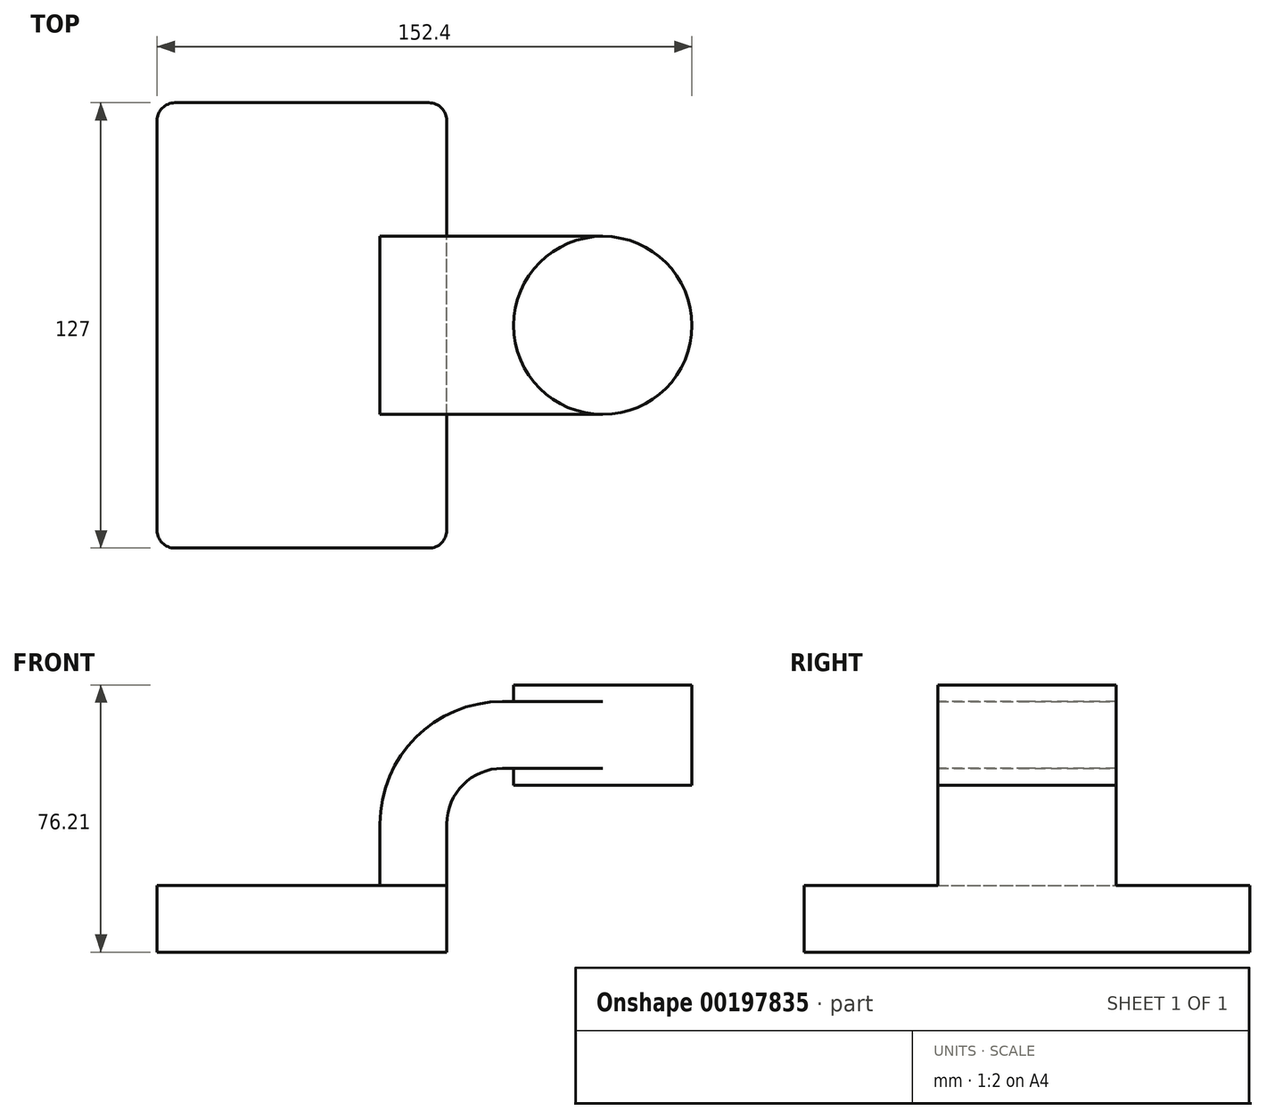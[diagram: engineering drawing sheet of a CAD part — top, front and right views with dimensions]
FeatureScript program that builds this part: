
annotation { "Feature Type Name" : "Feature", "Feature Type Description" : "" }
export const myFeature = defineFeature(function(context is Context, id is Id, definition is map)
    precondition{}
    {
        {
            var Q0;
            Q0=qCreatedBy(makeId("Front.planeOp"),FACE);
            var sketch = newSketch(context, id + "F0", { "sketchPlane" : qUnion([Q0])});
            skLineSegment(sketch, "E0.bottom", {"start": v(41.28, -9.52) * mm, "end": v(-41.27, -9.52) * mm});
            skLineSegment(sketch, "E0.top", {"start": v(41.27, 9.53) * mm, "end": v(-41.28, 9.53) * mm});
            skLineSegment(sketch, "E0.left", {"start": v(41.28, -9.52) * mm, "end": v(41.28, 9.53) * mm});
            skLineSegment(sketch, "E0.right", {"start": v(-41.27, -9.52) * mm, "end": v(-41.28, 9.53) * mm});
            skPoint(sketch, "E0.middle", {"position": v(0, 0) * mm});
            skLineSegment(sketch, "E1.bottom", {"start": v(111.12, 38.1) * mm, "end": v(60.32, 38.1) * mm});
            skLineSegment(sketch, "E1.top", {"start": v(111.12, 66.68) * mm, "end": v(60.32, 66.68) * mm});
            skLineSegment(sketch, "E1.left", {"start": v(111.12, 38.1) * mm, "end": v(111.12, 66.68) * mm});
            skLineSegment(sketch, "E1.right", {"start": v(60.32, 38.1) * mm, "end": v(60.32, 66.68) * mm});
            skPoint(sketch, "E1.middle", {"position": v(85.72, 52.39) * mm});
            skLineSegment(sketch, "E2", {"start": v(41.27, 9.53) * mm, "end": v(41.27, 27) * mm});
            skArc(sketch, "E3", {"start": v(41.27, 27) * mm, "mid": v(45.92, 38.23) * mm, "end": v(57.15, 42.88) * mm});
            skLineSegment(sketch, "E4", {"start": v(57.15, 42.88) * mm, "end": v(85.72, 42.88) * mm});
            skLineSegment(sketch, "E5.0", {"start": v(57.15, 61.93) * mm, "end": v(85.72, 61.93) * mm});
            skArc(sketch, "E5.1", {"start": v(22.23, 27) * mm, "mid": v(32.45, 51.7) * mm, "end": v(57.15, 61.93) * mm});
            skLineSegment(sketch, "E5.2", {"start": v(22.23, 9.53) * mm, "end": v(22.23, 27) * mm});
            skLineSegment(sketch, "E6", {"start": v(85.72, 38.1) * mm, "end": v(85.72, 66.68) * mm});
            skFitSpline(sketch, "E7", {"points": [v(-41.28, 9.53) * mm, v(57.15, 61.93) * mm], "startDerivative": vector(0.38, 74.3) * mm, "endDerivative": vector(122.95, -0.87) * mm});
            skSolve(sketch);
        }
        {
            var Q0;
            Q0=makeQuery(id+"F0.imprint","IMPRINT",FACE,{"disambiguationData":[TD([[makeQuery(id+"F0.imprint","IMPRINT",EDGE,{"derivedFrom":sQuery(id+"F0.wireOp",EDGE,"E0.bottom")}),-1.0]])]});
            extrude(context, id + "F1", {"entities" : qUnion([Q0]), "endBound" : BoundingType.SYMMETRIC, "depth" : 127 * mm});
        }
        {
            var Q0;
            {var subQ1=sQuery(id+"F0.wireOp",EDGE,"E2");Q0=makeQuery(id+"F0.imprint","IMPRINT",FACE,{"disambiguationData":[TD([[makeQuery(id+"F0.imprint","IMPRINT",EDGE,{"derivedFrom":subQ1}),1.0]])]});}
            var Q1;
            {var subQ0=sQuery(id+"F0.wireOp",EDGE,"E4");var subQ1=sQuery(id+"F0.wireOp",EDGE,"E1.right");var subQ2=makeQuery(id+"F0.imprint","INTERSECT",VERTEX,{"derivedFrom":[subQ1,subQ0]});Q1=makeQuery(id+"F0.imprint","IMPRINT",FACE,{"disambiguationData":[TD([[makeQuery(id+"F0.imprint","IMPRINT",EDGE,{"disambiguationData":[TD([[subQ2,-1.0]])],"derivedFrom":subQ1}),-1.0]])]});}
            extrude(context, id + "F2", {"entities" : qUnion([Q0, Q1]), "operationType" : NewBodyOperationType.ADD, "endBound" : BoundingType.SYMMETRIC, "depth" : 50.8 * mm});
        }
        {
            var Q0;
            Q0=makeQuery(id+"F0.imprint","IMPRINT",FACE,{"disambiguationData":[TD([[makeQuery(id+"F0.imprint","IMPRINT",EDGE,{"derivedFrom":sQuery(id+"F0.wireOp",EDGE,"E5.1")}),1.0]])]});
            extrude(context, id + "F3", {"entities" : qUnion([Q0]), "operationType" : NewBodyOperationType.ADD, "depth" : 15.88 * mm});
        }
        {
            var Q0;
            {var subQ0=sQuery(id+"F0.wireOp",EDGE,"E1.left");Q0=makeQuery(id+"F0.imprint","IMPRINT",FACE,{"disambiguationData":[TD([[makeQuery(id+"F0.imprint","IMPRINT",EDGE,{"derivedFrom":subQ0}),1.0]])]});}
            var Q1;
            Q1=sQuery(id+"F0.wireOp",EDGE,"E6");
            revolve(context, id + "F4", {"operationType" : NewBodyOperationType.ADD, "entities" : qUnion([Q0]), "axis" : qUnion([Q1]), "revolveType" : RevolveType.FULL});
        }
        {
            var Q0;
            Q0=makeQuery(id+"F1.opExtrude","CAP_EDGE",EDGE,{"disambiguationData":[OSD([sQuery(id+"F0.wireOp",EDGE,"E0.left")])],"isStart":false});
            var Q1;
            Q1=makeQuery(id+"F1.opExtrude","CAP_EDGE",EDGE,{"disambiguationData":[OSD([sQuery(id+"F0.wireOp",EDGE,"E0.right")])],"isStart":false});
            var Q2;
            Q2=makeQuery(id+"F1.opExtrude","CAP_EDGE",EDGE,{"disambiguationData":[OSD([sQuery(id+"F0.wireOp",EDGE,"E0.left")])],"isStart":true});
            var Q3;
            Q3=makeQuery(id+"F1.opExtrude","CAP_EDGE",EDGE,{"disambiguationData":[OSD([sQuery(id+"F0.wireOp",EDGE,"E0.right")])],"isStart":true});
            fillet(context, id + "F5", {"entities" : qUnion([Q0, Q1, Q2, Q3]), "radius" : 5.08 * mm, "tangentPropagation" : true, "allowEdgeOverflow" : false});
        }
    });
